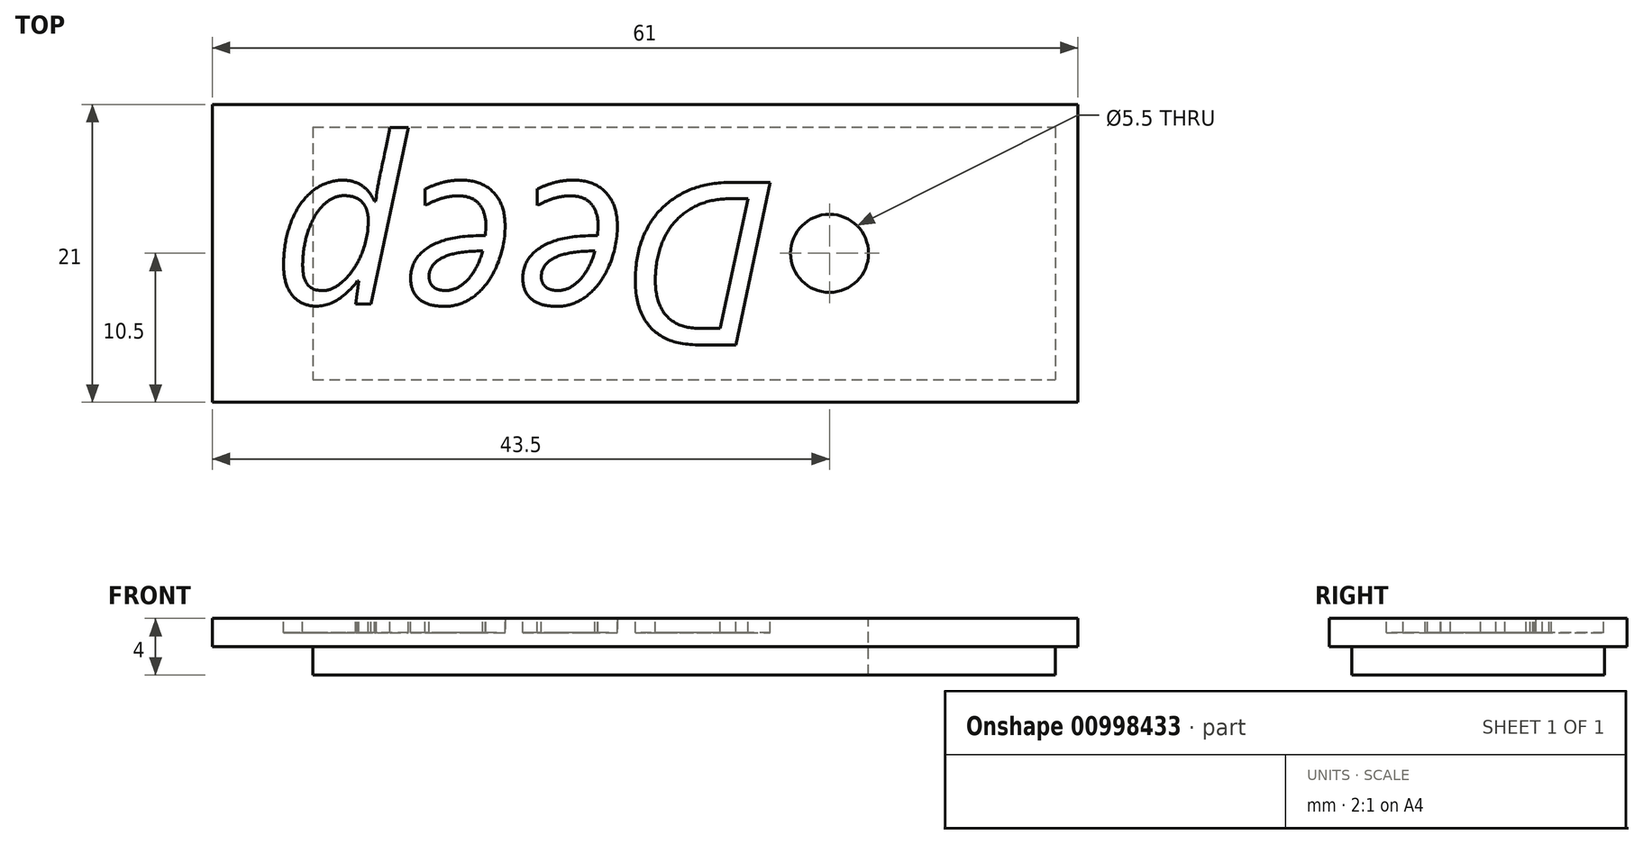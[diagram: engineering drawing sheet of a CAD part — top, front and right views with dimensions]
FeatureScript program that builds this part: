
annotation { "Feature Type Name" : "Feature", "Feature Type Description" : "" }
export const myFeature = defineFeature(function(context is Context, id is Id, definition is map)
    precondition{}
    {
        {
            var Q0;
            Q0=qCreatedBy(makeId("Top.planeOp"),FACE);
            var sketch = newSketch(context, id + "F0", { "sketchPlane" : qUnion([Q0])});
            skLineSegment(sketch, "E0.bottom", {"start": v(-26.15, 8.9) * mm, "end": v(26.15, 8.9) * mm});
            skLineSegment(sketch, "E0.top", {"start": v(-26.15, -8.9) * mm, "end": v(26.15, -8.9) * mm});
            skLineSegment(sketch, "E0.left", {"start": v(-26.15, 8.9) * mm, "end": v(-26.15, -8.9) * mm});
            skLineSegment(sketch, "E0.right", {"start": v(26.15, 8.9) * mm, "end": v(26.15, -8.9) * mm});
            skSolve(sketch);
        }
        {
            var Q0;
            Q0=makeQuery(id+"F0.imprint","IMPRINT",FACE,{"disambiguationData":[TD([[makeQuery(id+"F0.imprint","IMPRINT",EDGE,{"derivedFrom":sQuery(id+"F0.wireOp",EDGE,"E0.bottom")}),-1.0]])]});
            extrude(context, id + "F1", {"entities" : qUnion([Q0]), "depth" : 2 * mm, "offsetDistance" : 25 * mm});
        }
        {
            var Q0;
            Q0=makeQuery(id+"F1.opExtrude","CAP_FACE",FACE,{"disambiguationData":[OSD([sQuery(id+"F0.wireOp",EDGE,"E0.bottom"),sQuery(id+"F0.wireOp",EDGE,"E0.top"),sQuery(id+"F0.wireOp",EDGE,"E0.left"),sQuery(id+"F0.wireOp",EDGE,"E0.right")])],"isStart":false});
            var sketch = newSketch(context, id + "F2", { "sketchPlane" : qUnion([Q0])});
            skLineSegment(sketch, "E1.bottom", {"start": v(-33.25, 10.5) * mm, "end": v(27.75, 10.5) * mm});
            skLineSegment(sketch, "E1.top", {"start": v(-33.25, -10.5) * mm, "end": v(27.75, -10.5) * mm});
            skLineSegment(sketch, "E1.left", {"start": v(-33.25, 10.5) * mm, "end": v(-33.25, -10.5) * mm});
            skLineSegment(sketch, "E1.right", {"start": v(27.75, 10.5) * mm, "end": v(27.75, -10.5) * mm});
            skLineSegment(sketch, "E2.bottom", {"start": v(22.09, 10.5) * mm, "end": v(23.58, 10.5) * mm});
            skLineSegment(sketch, "E2.top", {"start": v(23.98, 0) * mm, "end": v(25.47, 0) * mm});
            skSolve(sketch);
        }
        {
            var Q0;
            Q0=makeQuery(id+"F2.imprint","IMPRINT",FACE,{"disambiguationData":[TD([[makeQuery(id+"F2.imprint","IMPRINT",EDGE,{"derivedFrom":makeQuery(id+"F1.opExtrude","CAP_EDGE",EDGE,{"disambiguationData":[OSD([sQuery(id+"F0.wireOp",EDGE,"E0.bottom")])],"isStart":false})}),-1.0]])]});
            var Q1;
            Q1=makeQuery(id+"F2.imprint","IMPRINT",FACE,{"disambiguationData":[TD([[makeQuery(id+"F2.imprint","IMPRINT",EDGE,{"derivedFrom":sQuery(id+"F2.wireOp",EDGE,"E1.top")}),1.0]])]});
            extrude(context, id + "F3", {"entities" : qUnion([Q0, Q1]), "operationType" : NewBodyOperationType.ADD, "depth" : 2 * mm, "offsetDistance" : 25 * mm});
        }
        {
            var Q0;
            Q0=makeQuery(id+"F3.opExtrude","CAP_FACE",FACE,{"disambiguationData":[OSD([sQuery(id+"F2.wireOp",EDGE,"E1.bottom"),sQuery(id+"F2.wireOp",EDGE,"E1.top"),sQuery(id+"F2.wireOp",EDGE,"E1.left"),sQuery(id+"F2.wireOp",EDGE,"E1.right"),sQuery(id+"F2.wireOp",EDGE,"E2.bottom")])],"isStart":false});
            var sketch = newSketch(context, id + "F4", { "sketchPlane" : qUnion([Q0])});
            skCircle(sketch, "E3", {"center": v(10.25, 0) * mm, "radius": 2.75 * mm});
            skSolve(sketch);
        }
        {
            var Q0;
            Q0=makeQuery(id+"F4.imprint","IMPRINT",FACE,{"disambiguationData":[TD([[makeQuery(id+"F4.imprint","IMPRINT",EDGE,{"derivedFrom":sQuery(id+"F4.wireOp",EDGE,"E3")}),1.0]])]});
            extrude(context, id + "F5", {"entities" : qUnion([Q0]), "operationType" : NewBodyOperationType.REMOVE, "endBound" : BoundingType.UP_TO_NEXT, "oppositeDirection" : true, "depth" : 25 * mm, "offsetDistance" : 25 * mm});
        }
        {
            var Q0;
            Q0=makeQuery(id+"F3.opExtrude","CAP_FACE",FACE,{"disambiguationData":[OSD([sQuery(id+"F2.wireOp",EDGE,"E1.bottom"),sQuery(id+"F2.wireOp",EDGE,"E1.top"),sQuery(id+"F2.wireOp",EDGE,"E1.left"),sQuery(id+"F2.wireOp",EDGE,"E1.right"),sQuery(id+"F2.wireOp",EDGE,"E2.bottom")])],"isStart":false});
            var sketch = newSketch(context, id + "F6", { "sketchPlane" : qUnion([Q0])});
            skText(sketch, "E4", { "text": "Deep", "fontName": "OpenSans-Italic.ttf"});
            const initialGuessF6  = {"E4": [0.00675, 0.005, -1, 0, 0.01155]};
            skSetInitialGuess(sketch, initialGuessF6);
            skSolve(sketch);
        }
        {
            var Q0;
            Q0=qSketchRegion(id+"F6",true);
            extrude(context, id + "F7", {"entities" : qUnion([Q0]), "operationType" : NewBodyOperationType.REMOVE, "oppositeDirection" : true, "depth" : 1 * mm, "offsetDistance" : 25 * mm});
        }
    });
